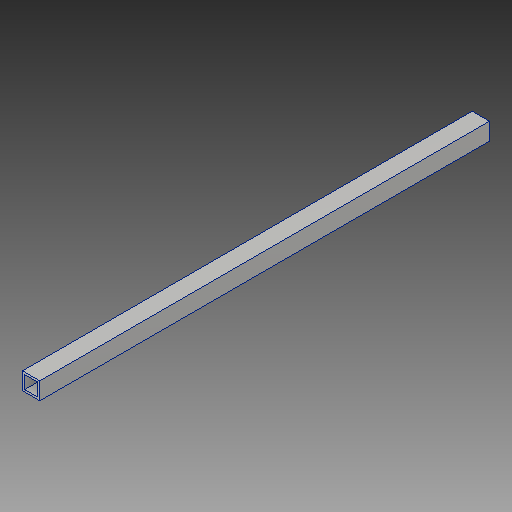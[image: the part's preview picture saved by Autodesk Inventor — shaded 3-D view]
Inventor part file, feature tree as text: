
AUTODESK INVENTOR PART (.ipt)
format: ipt  version: 2018 (Build 220112000, 112)  size: 105,984 bytes
history: native  units: in
note: dims shown in document units (in); Inventor stores cm internally (conversion verified against a paired STEP export)
features: extrude x2, sketch x2
ambient origin geometry x8: Origin, YZ Plane, XZ Plane, XY Plane, X Axis, Y Axis, Z Axis, Center Point
bodies: Solid1 (feature_tree)
feature tree (4):
  extrude  "Extrusion1"  Depth=26.0in
  extrude  "Extrusion2"  Depth=0.125in
  sketch  "Sketch1"  dims[d0=1.0in d1=26.0in]
  sketch  "Sketch2"  dims[d2=1.0in d3=0.0in d4=0.125in d5=0.125in d6=0.75in d7=0.75in d8=26.8125in d9=0.0in]
